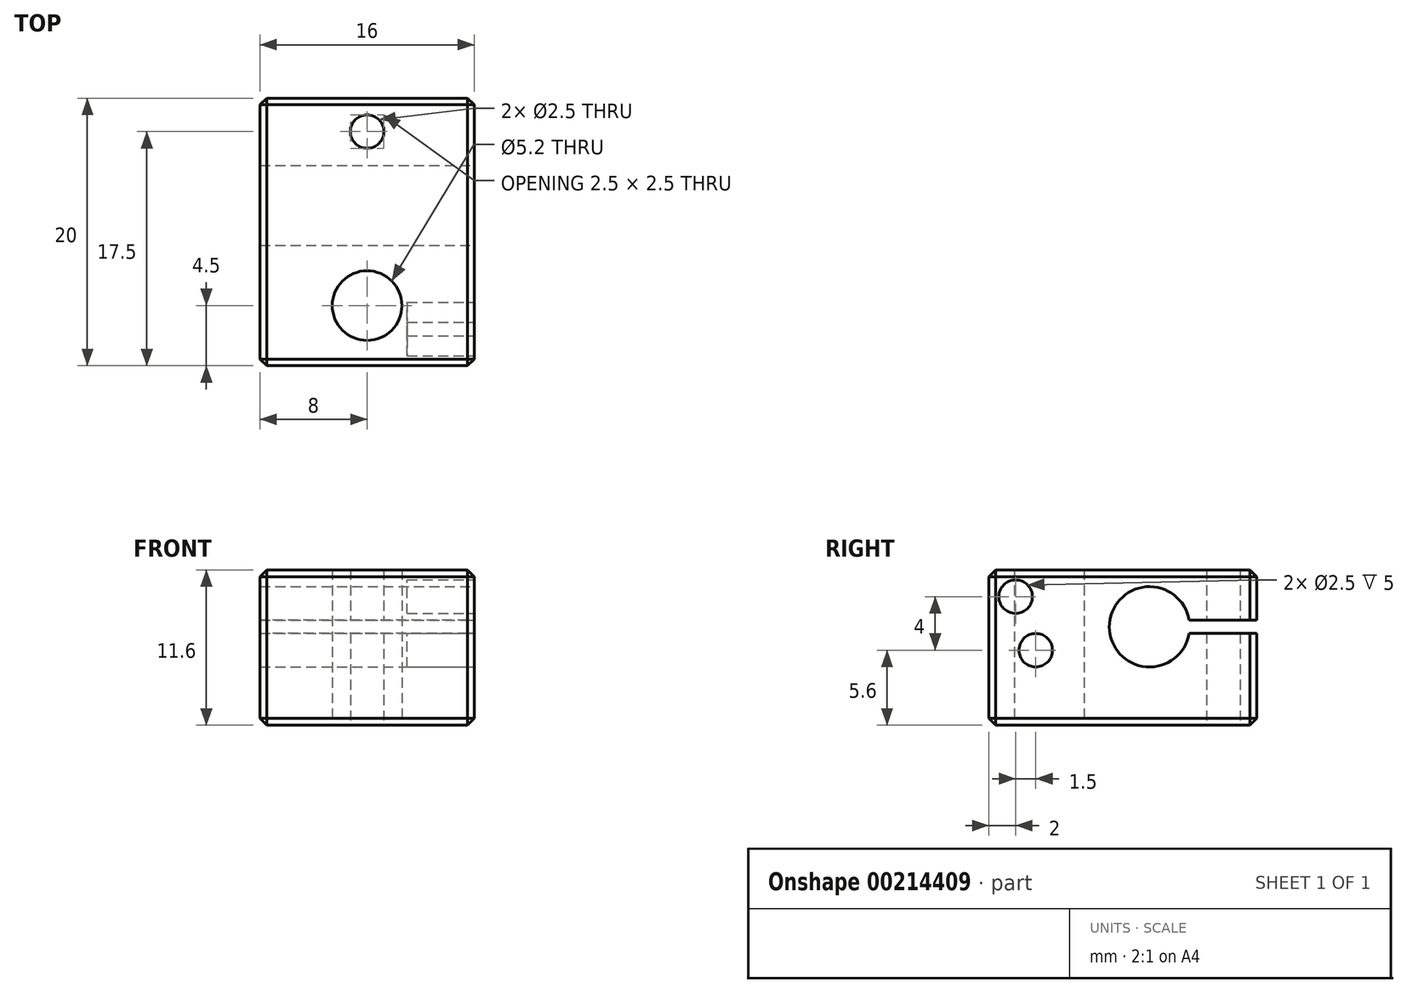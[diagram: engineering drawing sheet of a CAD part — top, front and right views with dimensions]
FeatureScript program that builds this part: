
annotation { "Feature Type Name" : "Feature", "Feature Type Description" : "" }
export const myFeature = defineFeature(function(context is Context, id is Id, definition is map)
    precondition{}
    {
        {
            var Q0;
            Q0=qCreatedBy(makeId("Top.planeOp"),FACE);
            var sketch = newSketch(context, id + "F0", { "sketchPlane" : qUnion([Q0])});
            skLineSegment(sketch, "E0.bottom", {"start": v(0, 0) * mm, "end": v(16, 0) * mm});
            skLineSegment(sketch, "E0.top", {"start": v(0, 20) * mm, "end": v(16, 20) * mm});
            skLineSegment(sketch, "E0.left", {"start": v(0, 0) * mm, "end": v(0, 20) * mm});
            skLineSegment(sketch, "E0.right", {"start": v(16, 0) * mm, "end": v(16, 20) * mm});
            skCircle(sketch, "E1", {"center": v(8, 4.5) * mm, "radius": 2.6 * mm});
            skCircle(sketch, "E2", {"center": v(8, 17.5) * mm, "radius": 1.25 * mm});
            skSolve(sketch);
        }
        {
            var Q0;
            Q0 = qSketchRegion(id + "F0", true);
            extrude(context, id + "F1", {"entities" : qUnion([Q0]), "depth" : 11.6 * mm});
        }
        {
            var Q0;
            Q0=makeQuery(id+"F1.opExtrude","SWEPT_FACE",FACE,{"disambiguationData":[OSD([sQuery(id+"F0.wireOp",EDGE,"E0.right")])]});
            var sketch = newSketch(context, id + "F2", { "sketchPlane" : qUnion([Q0])});
            skArc(sketch, "E3", {"start": v(14.96, 7.85) * mm, "mid": v(9, 7.35) * mm, "end": v(14.96, 6.85) * mm});
            skLineSegment(sketch, "E4", {"start": v(12, 7.35) * mm, "end": v(20, 7.35) * mm, "construction": true});
            skLineSegment(sketch, "E5.0", {"start": v(14.96, 6.85) * mm, "end": v(21.96, 6.85) * mm});
            skLineSegment(sketch, "E6.0", {"start": v(14.96, 7.85) * mm, "end": v(21.96, 7.85) * mm});
            skLineSegment(sketch, "E7", {"start": v(21.96, 7.85) * mm, "end": v(21.96, 6.85) * mm});
            skSolve(sketch);
        }
        {
            var Q0;
            Q0 = qSketchRegion(id + "F2", true);
            extrude(context, id + "F3", {"entities" : qUnion([Q0]), "operationType" : NewBodyOperationType.REMOVE, "endBound" : BoundingType.THROUGH_ALL, "oppositeDirection" : true, "depth" : 25 * mm});
        }
        {
            var Q0;
            Q0=makeQuery(id+"F1.opExtrude","SWEPT_FACE",FACE,{"disambiguationData":[OSD([sQuery(id+"F0.wireOp",EDGE,"E0.right")])]});
            var sketch = newSketch(context, id + "F4", { "sketchPlane" : qUnion([Q0])});
            skCircle(sketch, "E8", {"center": v(2, 9.6) * mm, "radius": 1.25 * mm});
            skCircle(sketch, "E9", {"center": v(3.5, 5.6) * mm, "radius": 1.25 * mm});
            skSolve(sketch);
        }
        {
            var Q0;
            Q0 = qSketchRegion(id + "F4", true);
            extrude(context, id + "F5", {"entities" : qUnion([Q0]), "operationType" : NewBodyOperationType.REMOVE, "oppositeDirection" : true, "depth" : 5 * mm});
        }
        {
            var Q0;
            Q0=makeQuery(id+"F1.opExtrude","SWEPT_FACE",FACE,{"disambiguationData":[OSD([sQuery(id+"F0.wireOp",EDGE,"E0.bottom")])]});
            var Q1;
            Q1=makeQuery(id+"F1.opExtrude","CAP_EDGE",EDGE,{"disambiguationData":[OSD([sQuery(id+"F0.wireOp",EDGE,"E0.right")])],"isStart":false});
            var Q2;
            Q2=makeQuery(id+"F1.opExtrude","CAP_EDGE",EDGE,{"disambiguationData":[OSD([sQuery(id+"F0.wireOp",EDGE,"E0.right")])],"isStart":true});
            var Q3;
            {var subQ0=sQuery(id+"F0.wireOp",EDGE,"E0.right");var subQ1=sQuery(id+"F0.wireOp",EDGE,"E0.top");Q3=makeQuery(id+"F3.boolean.opBoolean","SPLIT",EDGE,{"disambiguationData":[TD([makeQuery(id+"F3.opExtrude","SWEPT_FACE",FACE,{"disambiguationData":[OSD([sQuery(id+"F2.wireOp",EDGE,"E5.0")])]})])],"derivedFrom":makeQuery(id+"F1.opExtrude","SWEPT_EDGE",EDGE,{"disambiguationData":[OSD([subQ1,subQ0])]})});}
            var Q4;
            {var subQ0=sQuery(id+"F0.wireOp",EDGE,"E0.right");var subQ1=sQuery(id+"F0.wireOp",EDGE,"E0.top");Q4=makeQuery(id+"F3.boolean.opBoolean","SPLIT",EDGE,{"disambiguationData":[TD([makeQuery(id+"F3.opExtrude","SWEPT_FACE",FACE,{"disambiguationData":[OSD([sQuery(id+"F2.wireOp",EDGE,"E6.0")])]})])],"derivedFrom":makeQuery(id+"F1.opExtrude","SWEPT_EDGE",EDGE,{"disambiguationData":[OSD([subQ1,subQ0])]})});}
            var Q5;
            {var subQ0=sQuery(id+"F0.wireOp",EDGE,"E0.left");var subQ1=sQuery(id+"F0.wireOp",EDGE,"E0.top");Q5=makeQuery(id+"F3.boolean.opBoolean","SPLIT",EDGE,{"disambiguationData":[TD([makeQuery(id+"F3.opExtrude","SWEPT_FACE",FACE,{"disambiguationData":[OSD([sQuery(id+"F2.wireOp",EDGE,"E6.0")])]})])],"derivedFrom":makeQuery(id+"F1.opExtrude","SWEPT_EDGE",EDGE,{"disambiguationData":[OSD([subQ1,subQ0])]})});}
            var Q6;
            Q6=makeQuery(id+"F1.opExtrude","CAP_EDGE",EDGE,{"disambiguationData":[OSD([sQuery(id+"F0.wireOp",EDGE,"E0.top")])],"isStart":false});
            var Q7;
            Q7=makeQuery(id+"F1.opExtrude","CAP_EDGE",EDGE,{"disambiguationData":[OSD([sQuery(id+"F0.wireOp",EDGE,"E0.top")])],"isStart":true});
            var Q8;
            {var subQ0=sQuery(id+"F0.wireOp",EDGE,"E0.left");var subQ1=sQuery(id+"F0.wireOp",EDGE,"E0.top");Q8=makeQuery(id+"F3.boolean.opBoolean","SPLIT",EDGE,{"disambiguationData":[TD([makeQuery(id+"F3.opExtrude","SWEPT_FACE",FACE,{"disambiguationData":[OSD([sQuery(id+"F2.wireOp",EDGE,"E5.0")])]})])],"derivedFrom":makeQuery(id+"F1.opExtrude","SWEPT_EDGE",EDGE,{"disambiguationData":[OSD([subQ1,subQ0])]})});}
            var Q9;
            Q9=makeQuery(id+"F1.opExtrude","CAP_EDGE",EDGE,{"disambiguationData":[OSD([sQuery(id+"F0.wireOp",EDGE,"E0.left")])],"isStart":false});
            var Q10;
            Q10=makeQuery(id+"F1.opExtrude","CAP_EDGE",EDGE,{"disambiguationData":[OSD([sQuery(id+"F0.wireOp",EDGE,"E0.left")])],"isStart":true});
            chamfer(context, id + "F6", {"entities" : qUnion([Q0, Q1, Q2, Q3, Q4, Q5, Q6, Q7, Q8, Q9, Q10]), "width" : 0.5 * mm, "tangentPropagation" : true});
        }
    });
